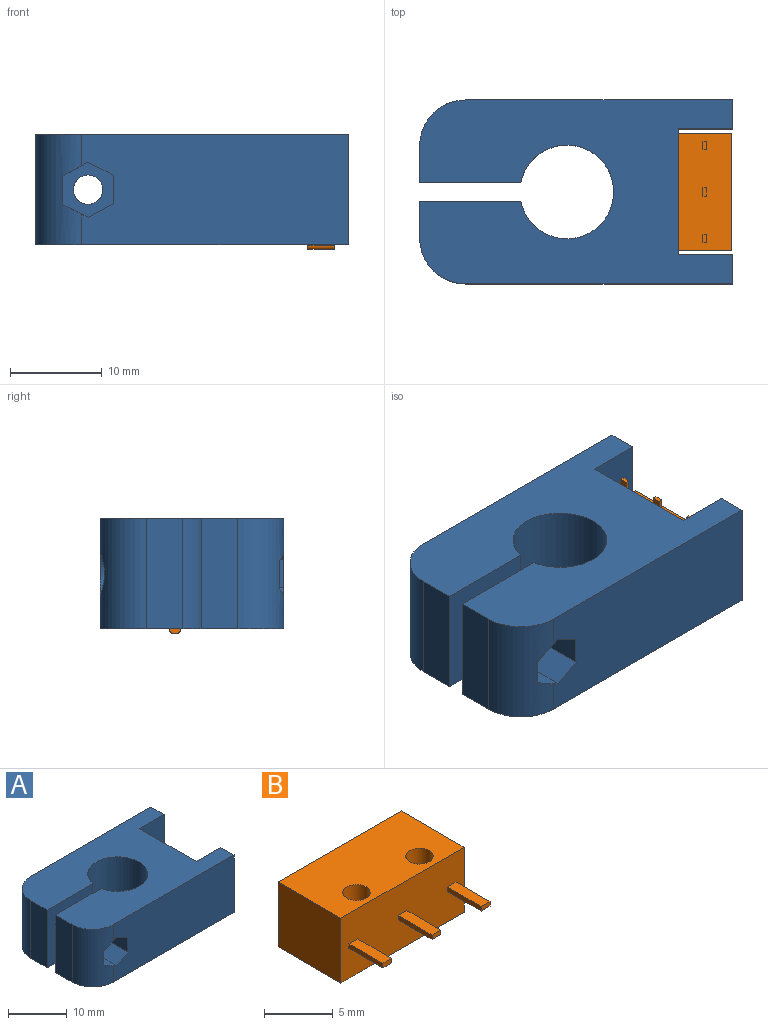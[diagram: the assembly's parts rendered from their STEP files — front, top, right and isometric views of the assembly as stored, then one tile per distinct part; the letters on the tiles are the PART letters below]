
ASSEMBLY  parts=2 mates=1
PART A: 31 faces, bbox 34x20x12 mm
  f0: cylinder r=1.6mm len=6mm, axis (0,-1,0), area 60.3mm2, adj f9,f27
  f1: plane 29x12mm, normal (0,-1,0), area 331.6mm2, adj f4,f6,f12,f21,f22,f24,f25,f26
  f2: cylinder r=1.6mm len=5mm, axis (0,-1,0), area 50.3mm2, adj f11,f20
  f3: plane 12x3.15mm, normal (1,0,0), area 37.8mm2, adj f4,f7,f12,f14
  f4: plane 34x20mm, normal (0,0,-1), area 484.9mm2, adj f1,f3,f5,f6,f7,f8,f9,f10
  f5: plane 12x4mm, normal (-1,0,0), area 48mm2, adj f4,f11,f12,f29
  f6: plane 12x3.15mm, normal (1,0,0), area 37.8mm2, adj f1,f4,f12,f15
  f7: plane 29x12mm, normal (0,1,0), area 331.8mm2, adj f3,f4,f12,f28,f30
  f8: plane 12x4mm, normal (-1,0,0), area 48mm2, adj f4,f9,f12,f30
  f9: plane 12x11mm, normal (0,-1,0), area 123.9mm2, adj f0,f4,f8,f10,f12
  f10: cylinder r=5.1mm len=12mm, axis (0,0,-1), area 360.4mm2, adj f4,f9,f11,f12
  f11: plane 12x11mm, normal (0,1,0), area 123.9mm2, adj f2,f4,f5,f10,f12
  f12: plane 34x20mm, normal (0,0,1), area 484.9mm2, adj f1,f3,f5,f6,f7,f8,f9,f10
  f13: plane 13.7x12mm, normal (1,0,0), area 158.7mm2, adj f4,f12,f14,f15,f16,f18
  f14: plane 12x5.9mm, normal (0,-1,0), area 70.8mm2, adj f3,f4,f12,f13
  f15: plane 12x5.9mm, normal (0,1,0), area 70.8mm2, adj f4,f6,f12,f13
  f16: cylinder r=0.95mm len=7mm, axis (1,0,0), area 41.8mm2, adj f13,f17
  f17: plane 1.9x1.9mm, normal (1,0,0), area 2.8mm2, adj f16
  f18: cylinder r=0.95mm len=7mm, axis (1,0,0), area 41.8mm2, adj f13,f19
  f19: plane 1.9x1.9mm, normal (1,0,0), area 2.8mm2, adj f18
  f20: plane 5.99x5.52mm, normal (0,-1,0), area 17mm2, adj f2,f21,f22,f23,f24,f25,f26
  f21: plane 4x2.77mm, normal (-0.45,0,-0.89), area 12.4mm2, adj f1,f20,f22,f26
  f22: plane 4.03x2.73mm, normal (0.49,0,-0.87), area 12.1mm2, adj f1,f20,f21,f23,f29
  f23: plane 3.56x3.11mm, normal (1,0,0), area 11.1mm2, adj f20,f22,f24,f29
  f24: plane 4.02x2.82mm, normal (0.44,0,0.9), area 12.1mm2, adj f1,f20,f23,f25,f29
  f25: plane 4x2.73mm, normal (-0.48,0,0.88), area 12.4mm2, adj f1,f20,f24,f26
  f26: plane 4x3.1mm, normal (-1,0,-0.02), area 12.4mm2, adj f1,f20,f21,f25
  f27: plane 5.6x5.6mm, normal (0,1,0), area 16.6mm2, adj f0,f28
  f28: cylinder r=2.8mm len=5.6mm, axis (0,1,0), area 51.1mm2, adj f7,f27,f30
  f29: cylinder r=5mm len=12mm, axis (0,0,-1), area 85.4mm2, adj f1,f4,f5,f12,f22,f23,f24
  f30: cylinder r=5mm len=12mm, axis (0,0,1), area 85.6mm2, adj f4,f7,f8,f12,f28
PART B: 30 faces, bbox 12.7x10.5x5.8 mm
  f0: plane 12.7x5.8mm, normal (0,-1,0), area 72.6mm2, adj f1,f2,f6,f7,f8,f10,f11,f12
  f1: plane 6.5x5.8mm, normal (-1,0,0), area 37.7mm2, adj f0,f5,f6,f7
  f2: plane 6.5x5.8mm, normal (1,0,0), area 37.7mm2, adj f0,f5,f6,f7
  f3: cylinder r=1mm len=5.8mm, axis (0,0,-1), area 36.4mm2, adj f6,f7
  f4: cylinder r=1mm len=5.8mm, axis (0,0,-1), area 36.4mm2, adj f6,f7
  f5: plane 12.7x5.8mm, normal (0,1,0), area 70.2mm2, adj f1,f2,f6,f7,f23,f24,f25,f26
  f6: plane 12.7x6.5mm, normal (0,0,1), area 76.3mm2, adj f0,f1,f2,f3,f4,f5
  f7: plane 12.7x6.5mm, normal (0,0,-1), area 76.3mm2, adj f0,f1,f2,f3,f4,f5
  f8: plane 3.5x0.4mm, normal (-1,0,0), area 1.4mm2, adj f0,f9,f11,f12
  f9: plane 0.9x0.4mm, normal (0,-1,0), area 0.4mm2, adj f8,f10,f11,f12
  f10: plane 3.5x0.4mm, normal (1,0,0), area 1.4mm2, adj f0,f9,f11,f12
  f11: plane 3.5x0.9mm, normal (0,0,1), area 3.2mm2, adj f0,f8,f9,f10
  f12: plane 3.5x0.9mm, normal (0,0,-1), area 3.2mm2, adj f0,f8,f9,f10
  f13: plane 3.5x0.4mm, normal (-1,0,0), area 1.4mm2, adj f0,f14,f16,f17
  f14: plane 0.9x0.4mm, normal (0,-1,0), area 0.4mm2, adj f13,f15,f16,f17
  f15: plane 3.5x0.4mm, normal (1,0,0), area 1.4mm2, adj f0,f14,f16,f17
  f16: plane 3.5x0.9mm, normal (0,0,1), area 3.1mm2, adj f0,f13,f14,f15
  f17: plane 3.5x0.9mm, normal (0,0,-1), area 3.1mm2, adj f0,f13,f14,f15
  f18: plane 3.5x0.4mm, normal (-1,0,0), area 1.4mm2, adj f0,f19,f21,f22
  f19: plane 0.9x0.4mm, normal (0,-1,0), area 0.4mm2, adj f18,f20,f21,f22
  f20: plane 3.5x0.4mm, normal (1,0,0), area 1.4mm2, adj f0,f19,f21,f22
  f21: plane 3.5x0.9mm, normal (0,0,1), area 3.2mm2, adj f0,f18,f19,f20
  f22: plane 3.5x0.9mm, normal (0,0,-1), area 3.2mm2, adj f0,f18,f19,f20
  f23: plane 2.9x0.1mm, normal (1,0,0), area 0.3mm2, adj f5,f24,f26,f29
  f24: plane 1.2x0.5mm, normal (0,0,-1), area 0.5mm2, adj f5,f23,f25,f27,f28,f29
  f25: plane 2.9x0.1mm, normal (-1,0,0), area 0.3mm2, adj f5,f24,f26,f28
  f26: plane 1.2x0.5mm, normal (0,0,1), area 0.5mm2, adj f5,f23,f25,f27,f28,f29
  f27: plane 2.9x0.4mm, normal (0,1,0), area 1.2mm2, adj f24,f26,f28,f29
  f28: cylinder r=0.4mm len=2.9mm, axis (0,0,-1), area 1.8mm2, adj f24,f25,f26,f27
  f29: cylinder r=0.4mm len=2.9mm, axis (0,0,1), area 1.8mm2, adj f23,f24,f26,f27
PLACE A t=(21.12,7.44,-16.8)mm
PLACE B rot(axis=(-0.58,0.58,-0.58),120deg) t=(33.22,7.44,-13.55)mm
MATE fastened A.f18 <-> B.f4  axis (1,0,0) through (33.22,4.19,-11.8)mm
